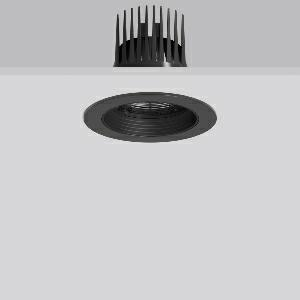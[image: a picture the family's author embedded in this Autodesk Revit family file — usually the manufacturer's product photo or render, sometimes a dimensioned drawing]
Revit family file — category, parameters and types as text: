
# Revit family: heledon_maxi_e_901761_003_1_76_b681
name_source: partatom
category: Lighting Fixtures
units: mm (PartAtom-declared; Revit-internal decimal feet)

## family parameters
Cut with Voids When Loaded = No
Host = Face
Light Source = No
Part Type = Normal
Room Calculation Point = No
Round Connector Dimension = Use Diameter
Shared = No

## types (1)
- HELEDON maxi E (1 x LED Modul 940, 2850 lm, 4000)
    Apparent Load = 25 VA
    Approval mark = CE
    CIE Flux Codes = 96 100 100 100 100
    Color Rendering = 92
    Color Temperature = 4000
    Default Elevation = 1800 mm
    Description = Series: HELEDON maxi
Round recessed downlight. Housing: die-cast aluminium, powder-coated. Black plastic ring and recessed LED to prevent glare from the side. Optical assembly with lens made of plastic (polycarbonate) for the best homogeneous light distribution - can be changed without tools. Best colour rendering index Ra>90. Suitable for Recessed ceiling mounting. Installation without tools thanks to spring fastening system. Including separate LED converter with connecting cable 600 mm.High quality converter without flickering and stroboscopic effect. Through-wiring box (5 pole) available as accessory. The following accessories can be mounted without use of tools: interchangeable lenses, decorative glasses, honeycomb louvre, clear and frosted diffusers, white interchangeable plastic ring. 
Colour: deep black, matt (RAL 9005)
Diameter: 162 mm
Height: 3 mm
Cut-out diameter: 152 mm
Recess height: 200 mm
Luminaire: recess height: 135 mm
Lamp: LED
Socket: without socket
Colour temperature: 4000K
Colour rendering index (CRI): 92
System power: 25 W
Rated luminous flux: 2850 lm
Luminous efficiency: 114 lm/W
Control gear: Converter, dimmable, DALI
Protection class: II
Type of protection: IP 20
    Height = 0 mm  [stored 0 ft]
    Lamp = 1 x LED Modul 940
    Lamp Light Flux = 2850 lm
    Lamp count = 1
    Length = 162 mm
    Lifetime = 50000 h
    Luminous efficacy = 114 lm/W
    Manufacturer = RZB
    ModVariant = No
    Model = 901761.003.1.76
    Mounting Place = Ceiling
    Mounting Type = Recessed
    Number of Poles = 1
    OnlyDefault = Yes
    Power Factor = 1
    Product Name = HELEDON maxi E
    Product group = Recessed downlights
    ProductGroupID = 402
    Protection Class = Protection class II
    Protection Degree = IP 20
    RLX_Detail_Level = 1
    RLX_Emergency_Light_Flux = 0 lm
    RLX_Emergency_Type = 0
    RLX_Emergency_Type_DB = No
    RlxData = <blob elided: 121017 chars, md5=90a1870d>
    Socket = socket
    Standby Power = 0 W
    System Light Flux = 2850 lm
    System Power = 25 W
    Type Comments = Product without accessories
    Type Image = 901663.003.jpg
    URL = http://relux.com
    VarID = ---
    Voltage = 230 V
    Voltage Range = 220-240 V
    Weight = 0.00 kg
    Width = 0 mm  [stored 0 ft]

note: [stored X ft] marks values corroborated as IEEE doubles in the binary element streams (Revit-internal decimal feet)

## geometry (parser evidence)
native form markers: Blend x4, Sweep x12
no freeform markers — native parametric forms only
